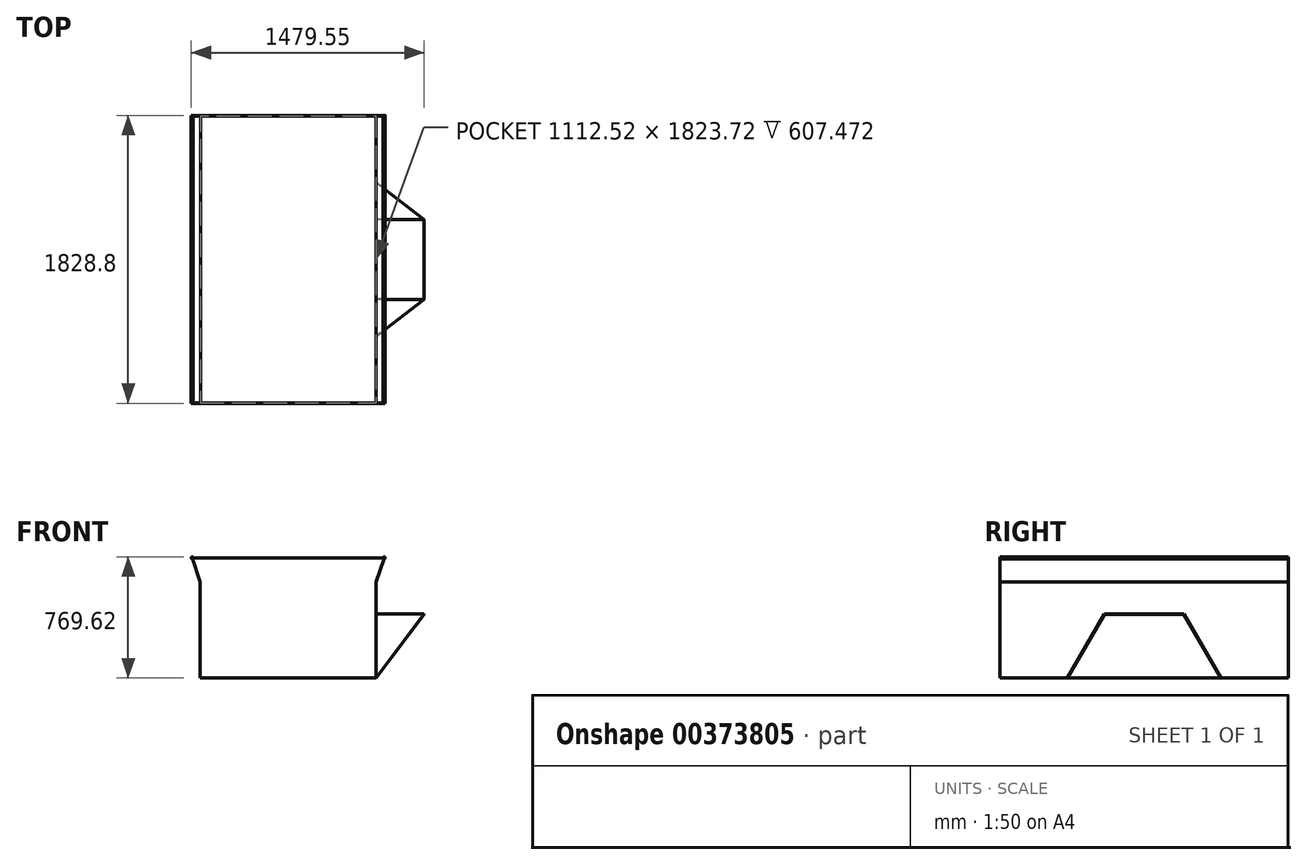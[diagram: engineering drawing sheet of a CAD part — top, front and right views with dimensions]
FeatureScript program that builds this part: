
annotation { "Feature Type Name" : "Feature", "Feature Type Description" : "" }
export const myFeature = defineFeature(function(context is Context, id is Id, definition is map)
    precondition{}
    {
        {
            var Q0;
            Q0=qCreatedBy(makeId("Front.planeOp"),FACE);
            var sketch = newSketch(context, id + "F0", { "sketchPlane" : qUnion([Q0])});
            skLineSegment(sketch, "E0.bottom", {"start": v(0, 0) * mm, "end": v(1117.6, 0) * mm});
            skLineSegment(sketch, "E0.left", {"start": v(0, 0) * mm, "end": v(0, 609.6) * mm});
            skLineSegment(sketch, "E0.right", {"start": v(1117.6, 0) * mm, "end": v(1117.6, 609.6) * mm});
            skLineSegment(sketch, "E1", {"start": v(-436.97, -421.83) * mm, "end": v(1391.83, -421.83) * mm});
            skLineSegment(sketch, "E2", {"start": v(-119.47, -421.83) * mm, "end": v(-119.47, -1073.34) * mm});
            skLineSegment(sketch, "E3", {"start": v(1074.33, -421.83) * mm, "end": v(1074.33, -1082.33) * mm});
            skPoint(sketch, "E4.startSnap0", {"position": v(558.8, 0) * mm});
            skLineSegment(sketch, "E5", {"start": v(558.8, 0) * mm, "end": v(558.8, 953.38) * mm, "construction": true});
            skLineSegment(sketch, "E6", {"start": v(558.8, 762) * mm, "end": v(1168.4, 762) * mm});
            skLineSegment(sketch, "E7", {"start": v(558.8, 762) * mm, "end": v(-50.8, 762) * mm});
            skLineSegment(sketch, "E8", {"start": v(1117.6, 609.6) * mm, "end": v(1168.4, 762) * mm});
            skLineSegment(sketch, "E9", {"start": v(0, 609.6) * mm, "end": v(-50.8, 762) * mm});
            skSolve(sketch);
        }
        {
            var Q0;
            Q0 = qSketchRegion(id + "F0", true);
            extrude(context, id + "F1", {"entities" : qUnion([Q0]), "oppositeDirection" : true, "depth" : 1828.8 * mm});
        }
        {
            var Q0;
            Q0=makeQuery(id+"F1.opExtrude","SWEPT_FACE",FACE,{"disambiguationData":[OSD([sQuery(id+"F0.wireOp",EDGE,"E6"),sQuery(id+"F0.wireOp",EDGE,"E7")])]});
            shell(context, id + "F2", {"entities" : qUnion([Q0]), "thickness" : 2.54 * mm});
        }
        {
            var Q0;
            Q0=makeQuery(id+"F1.opExtrude","CAP_FACE",FACE,{"disambiguationData":[OSD([sQuery(id+"F0.wireOp",EDGE,"E0.bottom"),sQuery(id+"F0.wireOp",EDGE,"E0.left"),sQuery(id+"F0.wireOp",EDGE,"E0.right"),sQuery(id+"F0.wireOp",EDGE,"E6"),sQuery(id+"F0.wireOp",EDGE,"E7"),sQuery(id+"F0.wireOp",EDGE,"E8"),sQuery(id+"F0.wireOp",EDGE,"E9")])],"isStart":true});
            var sketch = newSketch(context, id + "F3", { "sketchPlane" : qUnion([Q0])});
            skCircle(sketch, "E10", {"center": v(1168.4, 762) * mm, "radius": 6.35 * mm});
            skCircle(sketch, "E11", {"center": v(-50.8, 762) * mm, "radius": 6.35 * mm});
            skSolve(sketch);
        }
        {
            var Q0;
            {var subQ0=sQuery(id+"F3.wireOp",EDGE,"E10");var subQ3=makeQuery(id+"F1.opExtrude","CAP_EDGE",EDGE,{"disambiguationData":[OSD([sQuery(id+"F0.wireOp",EDGE,"E8")])],"isStart":true});var subQ4=makeQuery(id+"F3.imprint","INTERSECT",VERTEX,{"derivedFrom":[subQ3,subQ0]});Q0=makeQuery(id+"F3.imprint","IMPRINT",FACE,{"disambiguationData":[TD([[makeQuery(id+"F3.imprint","IMPRINT",EDGE,{"disambiguationData":[TD([[subQ4,-1.0]])],"derivedFrom":subQ0}),1.0]])]});}
            var Q1;
            {var subQ0=sQuery(id+"F3.wireOp",EDGE,"E11");var subQ3=makeQuery(id+"F1.opExtrude","CAP_EDGE",EDGE,{"disambiguationData":[OSD([sQuery(id+"F0.wireOp",EDGE,"E9")])],"isStart":true});var subQ4=makeQuery(id+"F3.imprint","INTERSECT",VERTEX,{"derivedFrom":[subQ3,subQ0]});Q1=makeQuery(id+"F3.imprint","IMPRINT",FACE,{"disambiguationData":[TD([[makeQuery(id+"F3.imprint","IMPRINT",EDGE,{"disambiguationData":[TD([[subQ4,1.0]])],"derivedFrom":subQ0}),1.0]])]});}
            var Q2;
            Q2=makeQuery(id+"F1.opExtrude","SWEPT_EDGE",EDGE,{"disambiguationData":[OSD([sQuery(id+"F0.wireOp",EDGE,"E7"),sQuery(id+"F0.wireOp",EDGE,"E9")])]});
            sweep(context, id + "F4", {"operationType" : NewBodyOperationType.ADD, "profiles" : qUnion([Q0, Q1]), "path" : qUnion([Q2])});
        }
        {
            var Q0;
            Q0=makeQuery(id+"F1.opExtrude","SWEPT_FACE",FACE,{"disambiguationData":[OSD([sQuery(id+"F0.wireOp",EDGE,"E0.right")])]});
            var sketch = newSketch(context, id + "F5", { "sketchPlane" : qUnion([Q0])});
            skPoint(sketch, "E12.endSnap0", {"position": v(914.4, 609.6) * mm});
            skLineSegment(sketch, "E13", {"start": v(914.4, 406.4) * mm, "end": v(1168.4, 406.4) * mm});
            skLineSegment(sketch, "E14", {"start": v(914.4, 406.4) * mm, "end": v(660.4, 406.4) * mm});
            skLineSegment(sketch, "E15", {"start": v(660.4, 406.4) * mm, "end": v(425.76, 0) * mm});
            skLineSegment(sketch, "E16", {"start": v(1168.4, 406.4) * mm, "end": v(1403.04, 0) * mm});
            skLineSegment(sketch, "E17.0", {"start": v(914.4, 403.86) * mm, "end": v(661.87, 403.86) * mm});
            skLineSegment(sketch, "E18.0", {"start": v(661.87, 403.86) * mm, "end": v(427.96, -1.27) * mm});
            skLineSegment(sketch, "E19.0", {"start": v(914.4, 403.86) * mm, "end": v(1166.93, 403.86) * mm});
            skLineSegment(sketch, "E20.0", {"start": v(1166.93, 403.86) * mm, "end": v(1400.84, -1.27) * mm});
            skLineSegment(sketch, "E21", {"start": v(427.96, -1.27) * mm, "end": v(425.76, 0) * mm});
            skLineSegment(sketch, "E22", {"start": v(1400.84, -1.27) * mm, "end": v(1403.04, 0) * mm});
            skSolve(sketch);
        }
        {
            var Q0;
            Q0 = qSketchRegion(id + "F5", true);
            extrude(context, id + "F6", {"entities" : qUnion([Q0]), "depth" : 304.8 * mm});
        }
        {
            var Q0;
            Q0=makeQuery(id+"F6.opExtrude","SWEPT_FACE",FACE,{"disambiguationData":[OSD([sQuery(id+"F5.wireOp",EDGE,"E15")])]});
            var sketch = newSketch(context, id + "F7", { "sketchPlane" : qUnion([Q0])});
            skLineSegment(sketch, "E23", {"start": v(1117.6, 212.88) * mm, "end": v(1422.4, 682.15) * mm});
            skSolve(sketch);
        }
        {
            var Q0;
            Q0=makeQuery(id+"F6.opExtrude","SWEPT_FACE",FACE,{"disambiguationData":[OSD([sQuery(id+"F5.wireOp",EDGE,"E16")])]});
            var sketch = newSketch(context, id + "F8", { "sketchPlane" : qUnion([Q0])});
            skLineSegment(sketch, "E24", {"start": v(-1422.4, -232.25) * mm, "end": v(-1117.6, -701.52) * mm});
            skSolve(sketch);
        }
        {
            var Q0;
            Q0 = qSketchRegion(id + "F8", true);
            var Q1;
            Q1=makeQuery(id+"F8.imprint","IMPRINT",FACE,{"disambiguationData":[TD([[makeQuery(id+"F8.imprint","IMPRINT",EDGE,{"derivedFrom":sQuery(id+"F8.wireOp",EDGE,"E24")}),-1.0]])]});
            extrude(context, id + "F9", {"entities" : qUnion([Q0, Q1]), "operationType" : NewBodyOperationType.REMOVE, "oppositeDirection" : true, "depth" : 25.4 * mm});
        }
        {
            var Q0;
            Q0=makeQuery(id+"F7.imprint","IMPRINT",FACE,{"disambiguationData":[TD([[makeQuery(id+"F7.imprint","IMPRINT",EDGE,{"derivedFrom":sQuery(id+"F7.wireOp",EDGE,"E23")}),-1.0]])]});
            extrude(context, id + "F10", {"entities" : qUnion([Q0]), "operationType" : NewBodyOperationType.REMOVE, "oppositeDirection" : true, "depth" : 25.4 * mm});
        }
    });
